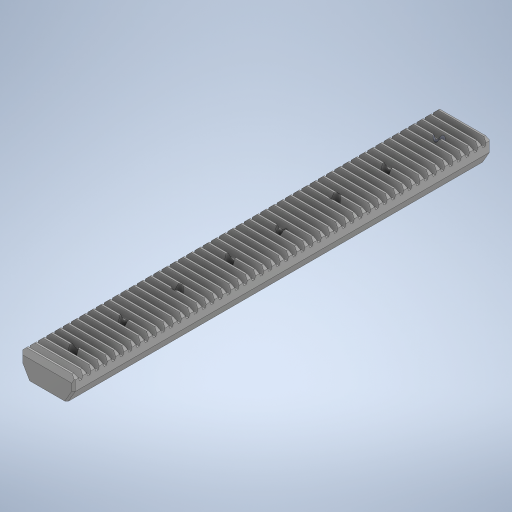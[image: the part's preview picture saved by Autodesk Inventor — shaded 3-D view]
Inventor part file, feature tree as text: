
AUTODESK INVENTOR PART (.ipt)
format: ipt  version: 2023.2 (Build 272271000, 271)  size: 1,355,776 bytes
history: native  units: mm
features: other x1, chamfer x1
ambient origin geometry x8: Origin, YZ Plane, XZ Plane, XY Plane, X Axis, Y Axis, Z Axis, Center Point
bodies: Solid1 (feature_tree)
feature tree (2):
  other  "39300B_TXM-Linear Slide Rail.STEP"
  chamfer  "Chamfer1"  [1 undecoded]
note: 1 required parameter value undecoded (feature->parameter linkage not recoverable at this tier; creation-order binding heuristic only, values carry confidence <= 0.55)
